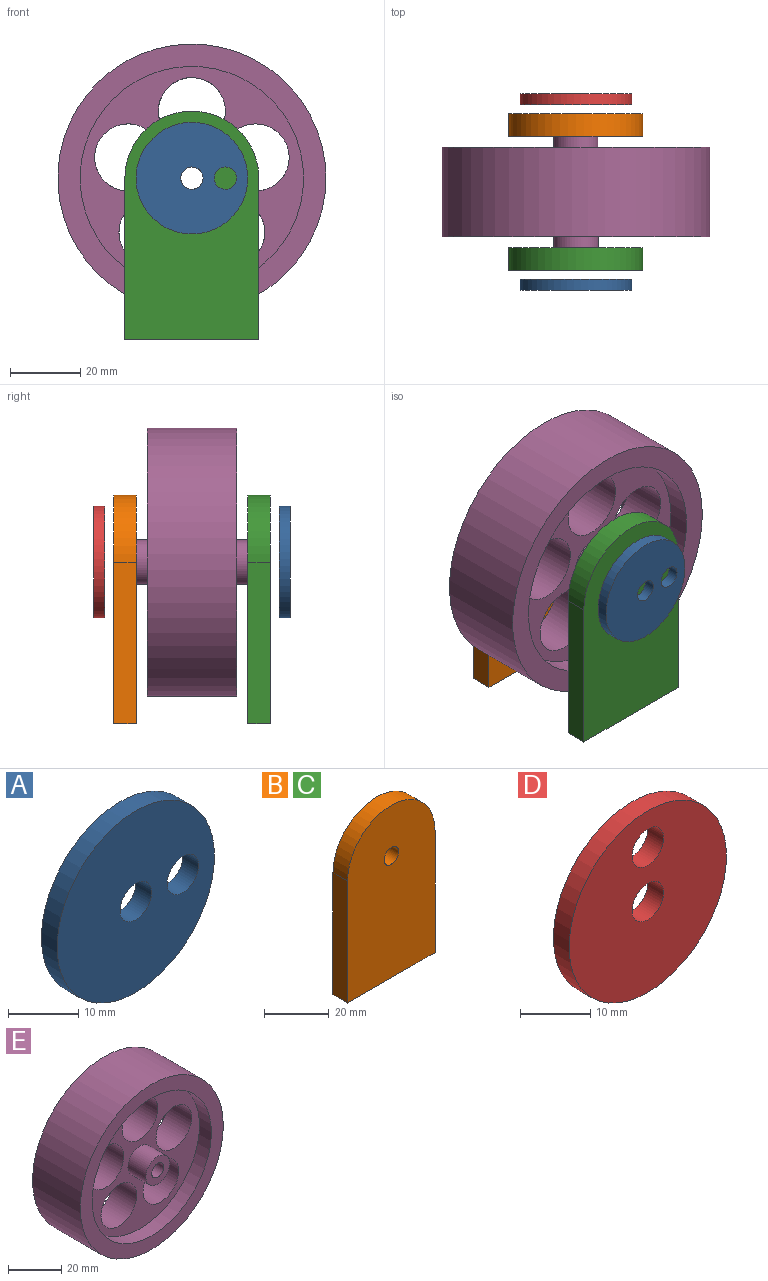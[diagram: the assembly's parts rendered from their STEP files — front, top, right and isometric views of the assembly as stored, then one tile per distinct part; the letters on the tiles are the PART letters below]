
ASSEMBLY  parts=5 mates=6
PART A: 5 faces, bbox 31.8x3.2x31.8 mm
  f0: cylinder r=3.17mm len=6.35mm, axis (0,1,0), area 63.3mm2, adj f3,f4
  f1: cylinder r=3.17mm len=6.35mm, axis (0,1,0), area 63.3mm2, adj f3,f4
  f2: cylinder r=15.88mm len=31.75mm, axis (0,1,0), area 316.7mm2, adj f3,f4
  f3: plane 31.75x31.75mm, normal (0,-1,0), area 728.4mm2, adj f0,f1,f2
  f4: plane 31.75x31.75mm, normal (0,1,0), area 728.4mm2, adj f0,f1,f2
PART B: 7 faces, bbox 38.1x6.4x65 mm
  f0: cylinder r=19.05mm len=38.1mm, axis (0,1,0), area 380mm2, adj f1,f4,f5,f6
  f1: plane 45.95x6.35mm, normal (-1,0,0), area 291.8mm2, adj f0,f2,f5,f6
  f2: plane 38.1x6.35mm, normal (0,0,-1), area 241.9mm2, adj f1,f4,f5,f6
  f3: cylinder r=3.17mm len=6.35mm, axis (0,1,0), area 126.7mm2, adj f5,f6
  f4: plane 45.95x6.35mm, normal (1,0,0), area 291.8mm2, adj f0,f2,f5,f6
  f5: plane 65x38.1mm, normal (0,-1,0), area 2289.2mm2, adj f0,f1,f2,f3,f4
  f6: plane 65x38.1mm, normal (0,1,0), area 2289.2mm2, adj f0,f1,f2,f3,f4
PART C: same geometry as B
PART D: 5 faces, bbox 31.8x3.2x31.8 mm
  f0: cylinder r=3.17mm len=6.35mm, axis (0,1,0), area 63.3mm2, adj f3,f4
  f1: cylinder r=3.17mm len=6.35mm, axis (0,1,0), area 63.3mm2, adj f3,f4
  f2: cylinder r=15.88mm len=31.75mm, axis (0,1,0), area 316.7mm2, adj f3,f4
  f3: plane 31.75x31.75mm, normal (0,-1,0), area 728.4mm2, adj f0,f1,f2
  f4: plane 31.75x31.75mm, normal (0,1,0), area 728.4mm2, adj f0,f1,f2
PART E: 17 faces, bbox 76.2x31.8x76.2 mm
  f0: cylinder r=38.1mm len=76.2mm, axis (0,1,0), area 6080.5mm2, adj f1,f2
  f1: plane 76.2x76.2mm, normal (0,-1,0), area 1393.4mm2, adj f0,f3
  f2: plane 76.2x76.2mm, normal (0,1,0), area 1393.4mm2, adj f0,f5
  f3: cylinder r=31.75mm len=63.5mm, axis (0,-1,0), area 1266.8mm2, adj f1,f4
  f4: plane 63.5x63.5mm, normal (0,-1,0), area 1615.1mm2, adj f3,f7,f8,f9,f10,f11,f12
  f5: cylinder r=31.75mm len=63.5mm, axis (0,1,0), area 1266.8mm2, adj f2,f6
  f6: plane 63.5x63.5mm, normal (0,1,0), area 1615.1mm2, adj f5,f7,f8,f9,f10,f11,f14
  f7: cylinder r=9.53mm len=19.05mm, axis (0,-1,0), area 760.1mm2, adj f4,f6
  f8: cylinder r=9.53mm len=19.05mm, axis (0,-1,0), area 760.1mm2, adj f4,f6
  f9: cylinder r=9.53mm len=19.05mm, axis (0,-1,0), area 760.1mm2, adj f4,f6
  f10: cylinder r=9.53mm len=19.05mm, axis (0,-1,0), area 760.1mm2, adj f4,f6
  f11: cylinder r=9.53mm len=19.05mm, axis (0,-1,0), area 760.1mm2, adj f4,f6
  f12: cylinder r=6.35mm len=12.7mm, axis (0,1,0), area 380mm2, adj f4,f13
  f13: plane 12.7x12.7mm, normal (0,-1,0), area 95mm2, adj f12,f16
  f14: cylinder r=6.35mm len=12.7mm, axis (0,-1,0), area 380mm2, adj f6,f15
  f15: plane 12.7x12.7mm, normal (0,1,0), area 95mm2, adj f14,f16
  f16: cylinder r=3.17mm len=31.75mm, axis (0,1,0), area 633.4mm2, adj f13,f15
PLACE A t=(-26.05,-30.34,16.45)mm
PLACE B t=(-26.05,16.65,16.45)mm fixed
PLACE C t=(-26.05,-21.45,16.45)mm fixed
PLACE D t=(-26.05,22.37,16.45)mm
PLACE E t=(-26.05,7.13,16.45)mm
MATE fastened D.f0 <-> B.f0  axis (0,-1,0) through (-26.05,19.19,16.45)mm
MATE planar C.f2 <-> B.f2  axis (0,0,-1) through (-26.05,-24.62,-29.5)mm
MATE fastened E.f0 <-> B.f0  axis (0,1,0) through (-26.05,10.3,16.45)mm
MATE fastened E.f0 <-> C.f0  axis (0,-1,0) through (-26.05,-21.45,16.45)mm
MATE fastened C.f0 <-> A.f0  axis (0,-1,0) through (-26.05,-27.8,16.45)mm
MATE planar C.f4 <-> B.f4  axis (1,0,0) through (-7,-24.62,-6.53)mm
